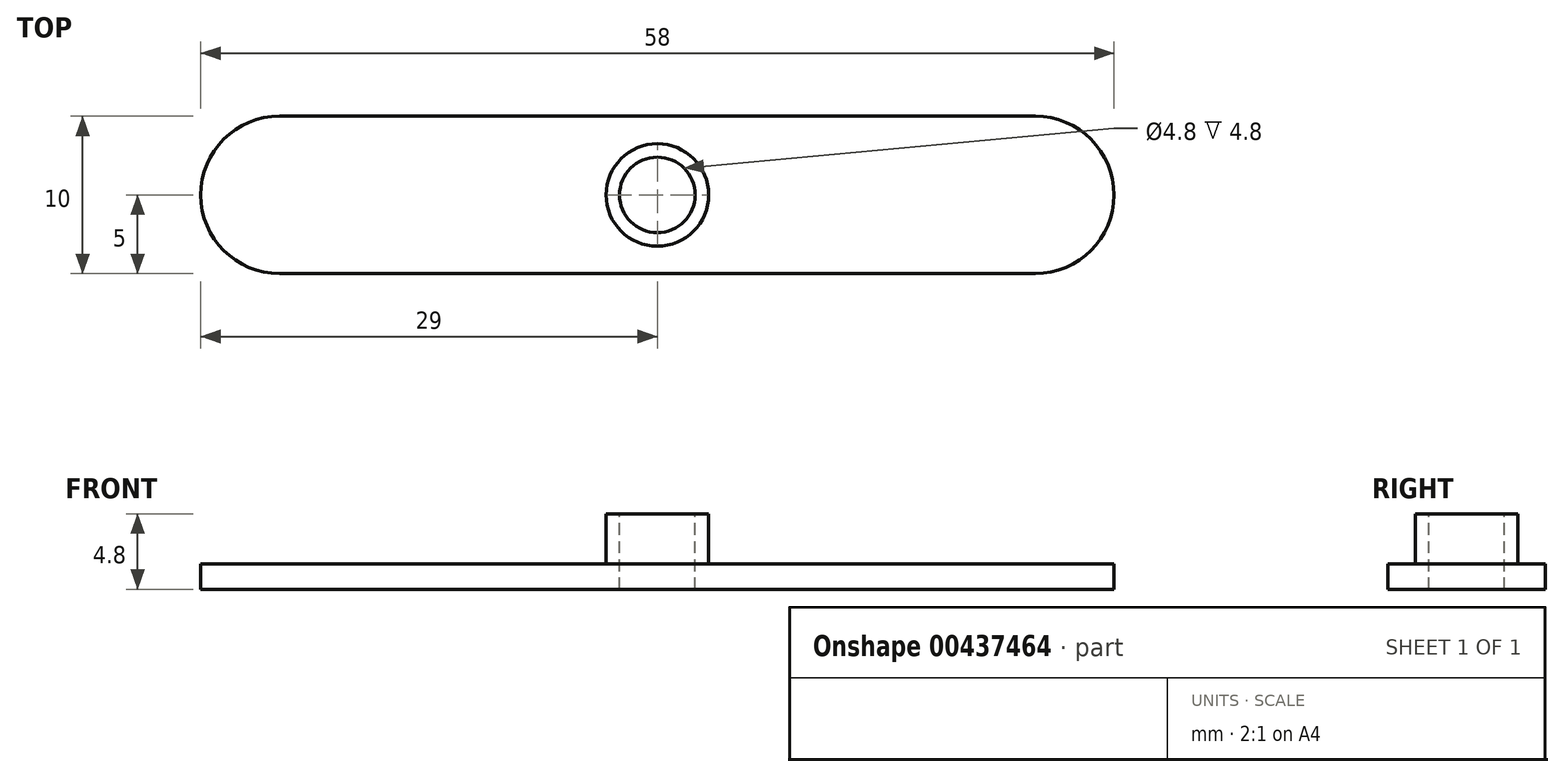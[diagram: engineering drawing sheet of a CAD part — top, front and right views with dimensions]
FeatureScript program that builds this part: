
annotation { "Feature Type Name" : "Feature", "Feature Type Description" : "" }
export const myFeature = defineFeature(function(context is Context, id is Id, definition is map)
    precondition{}
    {
        {
            var Q0;
            Q0=qCreatedBy(makeId("Top.planeOp"),FACE);
            var sketch = newSketch(context, id + "F0", { "sketchPlane" : qUnion([Q0])});
            skLineSegment(sketch, "E0.bottom", {"start": v(29, 5) * mm, "end": v(-29, 5) * mm});
            skLineSegment(sketch, "E0.top", {"start": v(29, -5) * mm, "end": v(-29, -5) * mm});
            skLineSegment(sketch, "E0.left", {"start": v(29, 5) * mm, "end": v(29, -5) * mm});
            skLineSegment(sketch, "E0.right", {"start": v(-29, 5) * mm, "end": v(-29, -5) * mm});
            skPoint(sketch, "E0.middle", {"position": v(0, 0) * mm});
            skCircle(sketch, "E1", {"center": v(0, 0) * mm, "radius": 2.4 * mm});
            skSolve(sketch);
        }
        {
            var Q0;
            Q0=makeQuery(id+"F0.imprint","IMPRINT",FACE,{"disambiguationData":[TD([[makeQuery(id+"F0.imprint","IMPRINT",EDGE,{"derivedFrom":sQuery(id+"F0.wireOp",EDGE,"E0.bottom")}),1.0]])]});
            extrude(context, id + "F1", {"entities" : qUnion([Q0]), "oppositeDirection" : true, "depth" : 1.6 * mm});
        }
        {
            var Q0;
            Q0=makeQuery(id+"F1.opExtrude","CAP_FACE",FACE,{"disambiguationData":[OSD([sQuery(id+"F0.wireOp",EDGE,"E0.bottom"),sQuery(id+"F0.wireOp",EDGE,"E0.top"),sQuery(id+"F0.wireOp",EDGE,"E0.left"),sQuery(id+"F0.wireOp",EDGE,"E0.right"),sQuery(id+"F0.wireOp",EDGE,"E1")])],"isStart":true});
            var sketch = newSketch(context, id + "F2", { "sketchPlane" : qUnion([Q0])});
            skCircle(sketch, "E2", {"center": v(0, 0) * mm, "radius": 3.25 * mm});
            skSolve(sketch);
        }
        {
            var Q0;
            Q0=makeQuery(id+"F2.imprint","IMPRINT",FACE,{"disambiguationData":[TD([[makeQuery(id+"F2.imprint","IMPRINT",EDGE,{"derivedFrom":sQuery(id+"F2.wireOp",EDGE,"E2")}),1.0]])]});
            extrude(context, id + "F3", {"entities" : qUnion([Q0]), "operationType" : NewBodyOperationType.ADD, "depth" : 3.2 * mm});
        }
        {
            var Q0;
            Q0=makeQuery(id+"F1.opExtrude","SWEPT_EDGE",EDGE,{"disambiguationData":[OSD([sQuery(id+"F0.wireOp",EDGE,"E0.bottom"),sQuery(id+"F0.wireOp",EDGE,"E0.left")])]});
            var Q1;
            Q1=makeQuery(id+"F1.opExtrude","SWEPT_EDGE",EDGE,{"disambiguationData":[OSD([sQuery(id+"F0.wireOp",EDGE,"E0.top"),sQuery(id+"F0.wireOp",EDGE,"E0.left")])]});
            var Q2;
            Q2=makeQuery(id+"F1.opExtrude","SWEPT_EDGE",EDGE,{"disambiguationData":[OSD([sQuery(id+"F0.wireOp",EDGE,"E0.bottom"),sQuery(id+"F0.wireOp",EDGE,"E0.right")])]});
            var Q3;
            Q3=makeQuery(id+"F1.opExtrude","SWEPT_EDGE",EDGE,{"disambiguationData":[OSD([sQuery(id+"F0.wireOp",EDGE,"E0.top"),sQuery(id+"F0.wireOp",EDGE,"E0.right")])]});
            fillet(context, id + "F4", {"entities" : qUnion([Q0, Q1, Q2, Q3]), "radius" : 5 * mm, "tangentPropagation" : true, "allowEdgeOverflow" : false});
        }
    });
